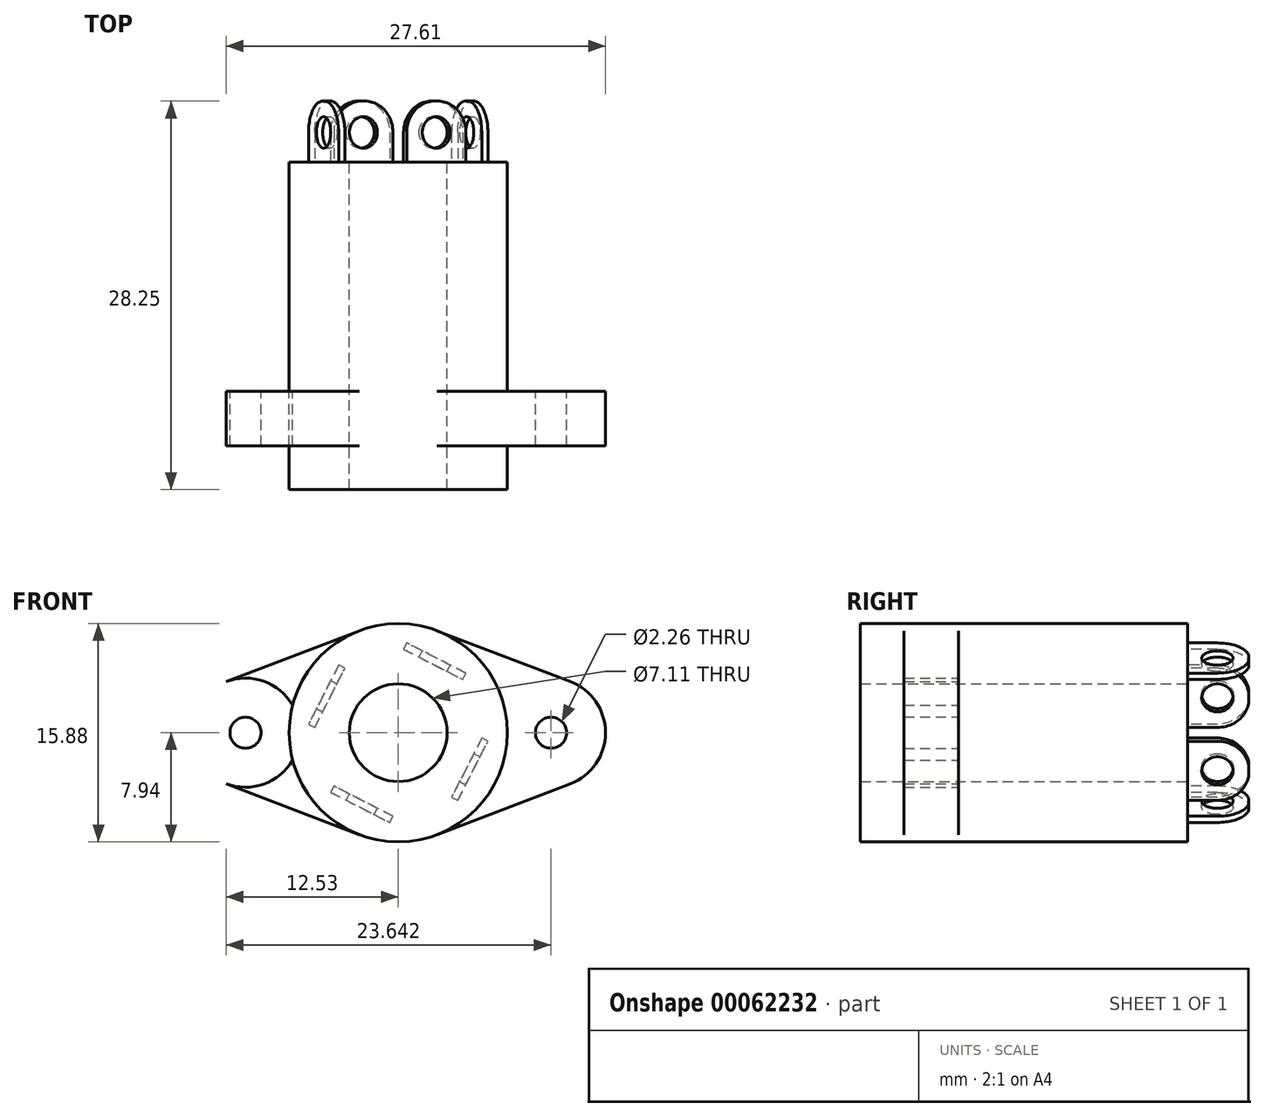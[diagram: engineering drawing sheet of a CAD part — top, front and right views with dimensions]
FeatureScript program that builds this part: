
annotation { "Feature Type Name" : "Feature", "Feature Type Description" : "" }
export const myFeature = defineFeature(function(context is Context, id is Id, definition is map)
    precondition{}
    {
        {
            var Q0;
            Q0=qCreatedBy(makeId("Front.planeOp"),FACE);
            var sketch = newSketch(context, id + "F0", { "sketchPlane" : qUnion([Q0])});
            skCircle(sketch, "E0", {"center": v(0, 0) * mm, "radius": 7.94 * mm});
            skCircle(sketch, "E1", {"center": v(11.11, 0) * mm, "radius": 3.97 * mm});
            skCircle(sketch, "E2", {"center": v(11.11, 0) * mm, "radius": 1.13 * mm});
            skCircle(sketch, "E3", {"center": v(0, 0) * mm, "radius": 3.56 * mm});
            skCircle(sketch, "E4.MirrorC", {"center": v(-11.11, 0) * mm, "radius": 1.13 * mm});
            skCircle(sketch, "E5.MirrorC", {"center": v(-11.11, 0) * mm, "radius": 3.97 * mm});
            skLineSegment(sketch, "E6", {"start": v(-12.53, 3.7) * mm, "end": v(-2.83, 7.41) * mm});
            skLineSegment(sketch, "E7", {"start": v(-12.53, -3.7) * mm, "end": v(-2.83, -7.41) * mm});
            skLineSegment(sketch, "E8", {"start": v(2.83, 7.41) * mm, "end": v(12.53, 3.7) * mm});
            skLineSegment(sketch, "E9", {"start": v(2.83, -7.41) * mm, "end": v(12.53, -3.7) * mm});
            skSolve(sketch);
        }
        {
            var Q0;
            Q0=makeQuery(id+"F0.imprint","IMPRINT",FACE,{"disambiguationData":[TD([[makeQuery(id+"F0.imprint","IMPRINT",EDGE,{"derivedFrom":sQuery(id+"F0.wireOp",EDGE,"E4.MirrorC")}),1.0]])]});
            var Q1;
            Q1=makeQuery(id+"F0.imprint","IMPRINT",FACE,{"disambiguationData":[TD([[makeQuery(id+"F0.imprint","IMPRINT",EDGE,{"derivedFrom":sQuery(id+"F0.wireOp",EDGE,"E2")}),-1.0]])]});
            var Q2;
            Q2=makeQuery(id+"F0.imprint","IMPRINT",FACE,{"disambiguationData":[TD([[makeQuery(id+"F0.imprint","IMPRINT",EDGE,{"derivedFrom":sQuery(id+"F0.wireOp",EDGE,"E3")}),-1.0]])]});
            var Q3;
            {var subQ0=sQuery(id+"F0.wireOp",EDGE,"E5.MirrorC");var subQ1=sQuery(id+"F0.wireOp",EDGE,"E0");var subQ2=makeQuery(id+"F0.imprint","INTERSECT",VERTEX,{"disambiguationData":[OD(0.0)],"derivedFrom":[subQ1,subQ0]});Q3=makeQuery(id+"F0.imprint","IMPRINT",FACE,{"disambiguationData":[TD([[makeQuery(id+"F0.imprint","IMPRINT",EDGE,{"disambiguationData":[TD([[subQ2,-1.0]])],"derivedFrom":subQ1}),1.0]])]});}
            var Q4;
            {var subQ0=sQuery(id+"F0.wireOp",EDGE,"E1");var subQ1=sQuery(id+"F0.wireOp",EDGE,"E0");var subQ2=makeQuery(id+"F0.imprint","INTERSECT",VERTEX,{"disambiguationData":[OD(0.0)],"derivedFrom":[subQ1,subQ0]});Q4=makeQuery(id+"F0.imprint","IMPRINT",FACE,{"disambiguationData":[TD([[makeQuery(id+"F0.imprint","IMPRINT",EDGE,{"disambiguationData":[TD([[subQ2,1.0]])],"derivedFrom":subQ1}),1.0]])]});}
            var Q5;
            {var subQ0=sQuery(id+"F0.wireOp",EDGE,"E8");Q5=makeQuery(id+"F0.imprint","IMPRINT",FACE,{"disambiguationData":[TD([[makeQuery(id+"F0.imprint","IMPRINT",EDGE,{"derivedFrom":subQ0}),-1.0]])]});}
            var Q6;
            {var subQ0=sQuery(id+"F0.wireOp",EDGE,"E6");Q6=makeQuery(id+"F0.imprint","IMPRINT",FACE,{"disambiguationData":[TD([[makeQuery(id+"F0.imprint","IMPRINT",EDGE,{"derivedFrom":subQ0}),-1.0]])]});}
            var Q7;
            {var subQ0=sQuery(id+"F0.wireOp",EDGE,"E7");Q7=makeQuery(id+"F0.imprint","IMPRINT",FACE,{"disambiguationData":[TD([[makeQuery(id+"F0.imprint","IMPRINT",EDGE,{"derivedFrom":subQ0}),1.0]])]});}
            var Q8;
            {var subQ0=sQuery(id+"F0.wireOp",EDGE,"E9");Q8=makeQuery(id+"F0.imprint","IMPRINT",FACE,{"disambiguationData":[TD([[makeQuery(id+"F0.imprint","IMPRINT",EDGE,{"derivedFrom":subQ0}),1.0]])]});}
            extrude(context, id + "F1", {"entities" : qUnion([Q0, Q1, Q2, Q3, Q4, Q5, Q6, Q7, Q8]), "depth" : 3.97 * mm});
        }
        {
            var Q0;
            Q0=makeQuery(id+"F1.opExtrude","CAP_FACE",FACE,{"disambiguationData":[OSD([sQuery(id+"F0.wireOp",EDGE,"E0"),sQuery(id+"F0.wireOp",EDGE,"E1"),sQuery(id+"F0.wireOp",EDGE,"E2"),sQuery(id+"F0.wireOp",EDGE,"E3"),sQuery(id+"F0.wireOp",EDGE,"E4.MirrorC"),sQuery(id+"F0.wireOp",EDGE,"E5.MirrorC"),sQuery(id+"F0.wireOp",EDGE,"E6"),sQuery(id+"F0.wireOp",EDGE,"E7"),sQuery(id+"F0.wireOp",EDGE,"E8"),sQuery(id+"F0.wireOp",EDGE,"E9")])],"isStart":false});
            var sketch = newSketch(context, id + "F2", { "sketchPlane" : qUnion([Q0])});
            skCircle(sketch, "E10.0", {"center": v(0, 0) * mm, "radius": 3.56 * mm});
            skCircle(sketch, "E11", {"center": v(0, 0) * mm, "radius": 7.94 * mm});
            skSolve(sketch);
        }
        {
            var Q0;
            Q0 = qSketchRegion(id + "F2", true);
            extrude(context, id + "F3", {"entities" : qUnion([Q0]), "operationType" : NewBodyOperationType.ADD, "depth" : 3.17 * mm, "hasSecondDirection" : true, "secondDirectionOppositeDirection" : true, "secondDirectionDepth" : 20.64 * mm});
        }
        {
            var Q0;
            Q0=makeQuery(id+"F3.opExtrude","CAP_FACE",FACE,{"disambiguationData":[OSD([sQuery(id+"F2.wireOp",EDGE,"E10.0"),sQuery(id+"F2.wireOp",EDGE,"E11")])],"isStart":true});
            var sketch = newSketch(context, id + "F4", { "sketchPlane" : qUnion([Q0])});
            skLineSegment(sketch, "E12", {"start": v(15.19, 14) * mm, "end": v(-15.95, -1.85) * mm, "construction": true});
            skCircle(sketch, "E13", {"center": v(0, 0) * mm, "radius": 5.59 * mm, "construction": true});
            skPoint(sketch, "E14", {"position": v(-2.54, 4.98) * mm});
            skLineSegment(sketch, "E15", {"start": v(-2.54, 4.98) * mm, "end": v(-4.69, 3.88) * mm});
            skLineSegment(sketch, "E16", {"start": v(-4.69, 3.88) * mm, "end": v(-4.92, 4.34) * mm});
            skLineSegment(sketch, "E17", {"start": v(-4.92, 4.34) * mm, "end": v(-0.62, 6.53) * mm});
            skLineSegment(sketch, "E18", {"start": v(-0.62, 6.53) * mm, "end": v(-0.39, 6.07) * mm});
            skLineSegment(sketch, "E19", {"start": v(-0.39, 6.07) * mm, "end": v(-2.54, 4.98) * mm});
            skLineSegment(sketch, "E20.1.0", {"start": v(-6.53, -0.62) * mm, "end": v(-6.07, -0.39) * mm});
            skLineSegment(sketch, "E20.1.1", {"start": v(-4.34, -4.92) * mm, "end": v(-6.53, -0.62) * mm});
            skLineSegment(sketch, "E20.1.2", {"start": v(-3.88, -4.69) * mm, "end": v(-4.34, -4.92) * mm});
            skLineSegment(sketch, "E20.1.3", {"start": v(-4.98, -2.54) * mm, "end": v(-3.88, -4.69) * mm});
            skLineSegment(sketch, "E20.1.4", {"start": v(-6.07, -0.39) * mm, "end": v(-4.98, -2.54) * mm});
            skPoint(sketch, "E20.1.5", {"position": v(-4.98, -2.54) * mm});
            skLineSegment(sketch, "E20.2.0", {"start": v(0.62, -6.53) * mm, "end": v(0.39, -6.07) * mm});
            skLineSegment(sketch, "E20.2.1", {"start": v(4.92, -4.34) * mm, "end": v(0.62, -6.53) * mm});
            skLineSegment(sketch, "E20.2.2", {"start": v(4.69, -3.88) * mm, "end": v(4.92, -4.34) * mm});
            skLineSegment(sketch, "E20.2.3", {"start": v(2.54, -4.98) * mm, "end": v(4.69, -3.88) * mm});
            skLineSegment(sketch, "E20.2.4", {"start": v(0.39, -6.07) * mm, "end": v(2.54, -4.98) * mm});
            skPoint(sketch, "E20.2.5", {"position": v(2.54, -4.98) * mm});
            skLineSegment(sketch, "E20.3.0", {"start": v(6.53, 0.62) * mm, "end": v(6.07, 0.39) * mm});
            skLineSegment(sketch, "E20.3.1", {"start": v(4.34, 4.92) * mm, "end": v(6.53, 0.62) * mm});
            skLineSegment(sketch, "E20.3.2", {"start": v(3.88, 4.69) * mm, "end": v(4.34, 4.92) * mm});
            skLineSegment(sketch, "E20.3.3", {"start": v(4.98, 2.54) * mm, "end": v(3.88, 4.69) * mm});
            skLineSegment(sketch, "E20.3.4", {"start": v(6.07, 0.39) * mm, "end": v(4.98, 2.54) * mm});
            skPoint(sketch, "E20.3.5", {"position": v(4.98, 2.54) * mm});
            skSolve(sketch);
        }
        {
            var Q0;
            Q0 = qSketchRegion(id + "F4", true);
            extrude(context, id + "F5", {"entities" : qUnion([Q0]), "operationType" : NewBodyOperationType.ADD, "depth" : 4.44 * mm});
        }
        {
            var Q0;
            Q0=makeQuery(id+"F5.opExtrude","SWEPT_FACE",FACE,{"disambiguationData":[OSD([sQuery(id+"F4.wireOp",EDGE,"E17")])]});
            var sketch = newSketch(context, id + "F6", { "sketchPlane" : qUnion([Q0])});
            skLineSegment(sketch, "E21.0.0", {"start": v(-2.41, 16.67) * mm, "end": v(2.41, 16.67) * mm});
            skLineSegment(sketch, "E21.0.1", {"start": v(2.41, 16.67) * mm, "end": v(2.41, 18.83) * mm});
            skLineSegment(sketch, "E21.0.2", {"start": v(0.13, 21.11) * mm, "end": v(-0.13, 21.11) * mm});
            skLineSegment(sketch, "E21.0.3", {"start": v(-2.41, 18.83) * mm, "end": v(-2.41, 16.67) * mm});
            skPoint(sketch, "E22.visualSharp", {"position": v(-2.41, 21.11) * mm});
            skArc(sketch, "E22.filletArc", {"start": v(-0.13, 21.11) * mm, "mid": v(-1.74, 20.44) * mm, "end": v(-2.41, 18.83) * mm});
            skPoint(sketch, "E23.visualSharp", {"position": v(2.41, 21.11) * mm});
            skArc(sketch, "E23.filletArc", {"start": v(2.41, 18.83) * mm, "mid": v(1.74, 20.44) * mm, "end": v(0.13, 21.11) * mm});
            skCircle(sketch, "E24", {"center": v(0, 18.83) * mm, "radius": 1.14 * mm});
            skSolve(sketch);
        }
        {
            var Q0;
            {var subQ0=sQuery(id+"F6.wireOp",EDGE,"E22.filletArc");Q0=makeQuery(id+"F6.imprint","IMPRINT",FACE,{"disambiguationData":[TD([[makeQuery(id+"F6.imprint","IMPRINT",EDGE,{"derivedFrom":subQ0}),-1.0]])]});}
            var Q1;
            Q1=makeQuery(id+"F6.imprint","IMPRINT",FACE,{"disambiguationData":[TD([[makeQuery(id+"F6.imprint","IMPRINT",EDGE,{"derivedFrom":sQuery(id+"F6.wireOp",EDGE,"E24")}),1.0]])]});
            var Q2;
            {var subQ0=sQuery(id+"F6.wireOp",EDGE,"E23.filletArc");Q2=makeQuery(id+"F6.imprint","IMPRINT",FACE,{"disambiguationData":[TD([[makeQuery(id+"F6.imprint","IMPRINT",EDGE,{"derivedFrom":subQ0}),-1.0]])]});}
            extrude(context, id + "F7", {"entities" : qUnion([Q0, Q1, Q2]), "operationType" : NewBodyOperationType.REMOVE, "endBound" : BoundingType.THROUGH_ALL, "oppositeDirection" : true, "depth" : 25.4 * mm});
        }
        {
            var Q0;
            Q0=makeQuery(id+"F5.opExtrude","SWEPT_FACE",FACE,{"disambiguationData":[OSD([sQuery(id+"F4.wireOp",EDGE,"E20.1.1")])]});
            var sketch = newSketch(context, id + "F8", { "sketchPlane" : qUnion([Q0])});
            skLineSegment(sketch, "E25.0", {"start": v(21.11, 2.41) * mm, "end": v(16.67, 2.41) * mm});
            skLineSegment(sketch, "E26.0.0", {"start": v(16.67, 2.41) * mm, "end": v(16.67, -2.41) * mm});
            skLineSegment(sketch, "E26.0.1", {"start": v(16.67, -2.41) * mm, "end": v(18.83, -2.41) * mm});
            skLineSegment(sketch, "E26.0.2", {"start": v(21.11, -0.13) * mm, "end": v(21.11, 0.13) * mm});
            skLineSegment(sketch, "E26.0.3", {"start": v(18.83, 2.41) * mm, "end": v(16.67, 2.41) * mm});
            skPoint(sketch, "E27.visualSharp", {"position": v(21.11, 2.41) * mm});
            skArc(sketch, "E27.filletArc", {"start": v(21.11, 0.13) * mm, "mid": v(20.44, 1.74) * mm, "end": v(18.83, 2.41) * mm});
            skPoint(sketch, "E28.visualSharp", {"position": v(21.11, -2.41) * mm});
            skArc(sketch, "E28.filletArc", {"start": v(18.83, -2.41) * mm, "mid": v(20.44, -1.74) * mm, "end": v(21.11, -0.13) * mm});
            skCircle(sketch, "E29", {"center": v(18.83, 0) * mm, "radius": 1.14 * mm});
            skSolve(sketch);
        }
        {
            var Q0;
            {var subQ0=sQuery(id+"F8.wireOp",EDGE,"E25.0");Q0=makeQuery(id+"F8.imprint","IMPRINT",FACE,{"disambiguationData":[TD([[makeQuery(id+"F8.imprint","IMPRINT",EDGE,{"derivedFrom":subQ0}),1.0]])]});}
            var Q1;
            Q1=makeQuery(id+"F8.imprint","IMPRINT",FACE,{"disambiguationData":[TD([[makeQuery(id+"F8.imprint","IMPRINT",EDGE,{"derivedFrom":sQuery(id+"F8.wireOp",EDGE,"E29")}),1.0]])]});
            var Q2;
            {var subQ0=sQuery(id+"F8.wireOp",EDGE,"E28.filletArc");Q2=makeQuery(id+"F8.imprint","IMPRINT",FACE,{"disambiguationData":[TD([[makeQuery(id+"F8.imprint","IMPRINT",EDGE,{"derivedFrom":subQ0}),-1.0]])]});}
            extrude(context, id + "F9", {"entities" : qUnion([Q0, Q1, Q2]), "operationType" : NewBodyOperationType.REMOVE, "endBound" : BoundingType.THROUGH_ALL, "oppositeDirection" : true, "depth" : 25.4 * mm});
        }
    });
